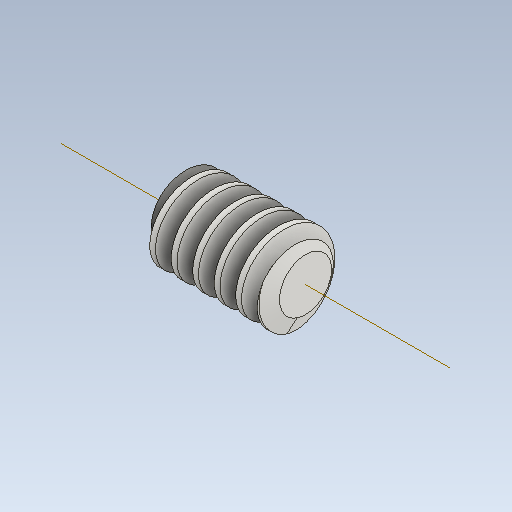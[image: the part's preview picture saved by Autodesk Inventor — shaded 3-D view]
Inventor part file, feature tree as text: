
AUTODESK INVENTOR PART (.ipt)
format: ipt  version: 2021.1 (Build 251245010, 245A)  size: 271,360 bytes
history: native  units: mm (DEFAULTED — no unit token found)
features: other x6, chamfer x2, pattern_circular x2, extrude x1, sketch x1
ambient origin geometry x6: Origin, XZ Plane, X Axis, Y Axis, Z Axis, Center Point
bodies: Solid1 (feature_tree)
feature tree (12):
  extrude  "Base Body"  Depth=10.0mm
  chamfer  "Chamfer1"  Distance=25.4mm
  chamfer  "Chamfer2"  [1 undecoded]
  other  "Tooth Sketch"
  other  "Left Tooth"
  pattern_circular  "Left Tooth Pattern"  [2 undecoded]
  other  "Tooth"
  pattern_circular  "Tooth Pattern"  [2 undecoded]
  other  "Base Body Sketch"
  sketch  "Sketch5"  dims[d4=40.0mm d5=16.493545mm d6=25.4mm d7=0.0mm d8=1.100579mm d9=3.023817mm d10=1.100579mm d11=3.023817mm d12=19.198622mm d14=3.1425mm d24=19.198622mm d25=15.113mm d26=1.0795mm d27=5.222956mm d28=6.87231mm d29=8.32924mm d30=4.318mm d31=10.0mm d32=80.0mm d33=0.0mm d34=90.0deg d35=90.0deg d36=0.0mm d37=0.0mm d43=10.0mm d45=360.0deg d46=45.0deg d47=45.0deg d49=0.0mm d53=0.0mm d54=48.106173mm d55=0.0mm d56=0.0mm d57=13.744621mm d58=25.4mm d59=0.0mm d60=4.318mm d61=25.4mm d62=80.0mm d63=0.0mm d64=90.0deg d65=90.0deg d66=0.0mm d67=0.0mm d68=10.0mm d69=10.0mm d70=360.0deg d72=10.0mm d74=10.0mm d75=10.0mm d76=0.0mm d77=48.106173mm]
  other  "Srf1"
  other  "Pitch Diameter"
note: 5 required parameter values undecoded (feature->parameter linkage not recoverable at this tier; creation-order binding heuristic only, values carry confidence <= 0.55)
